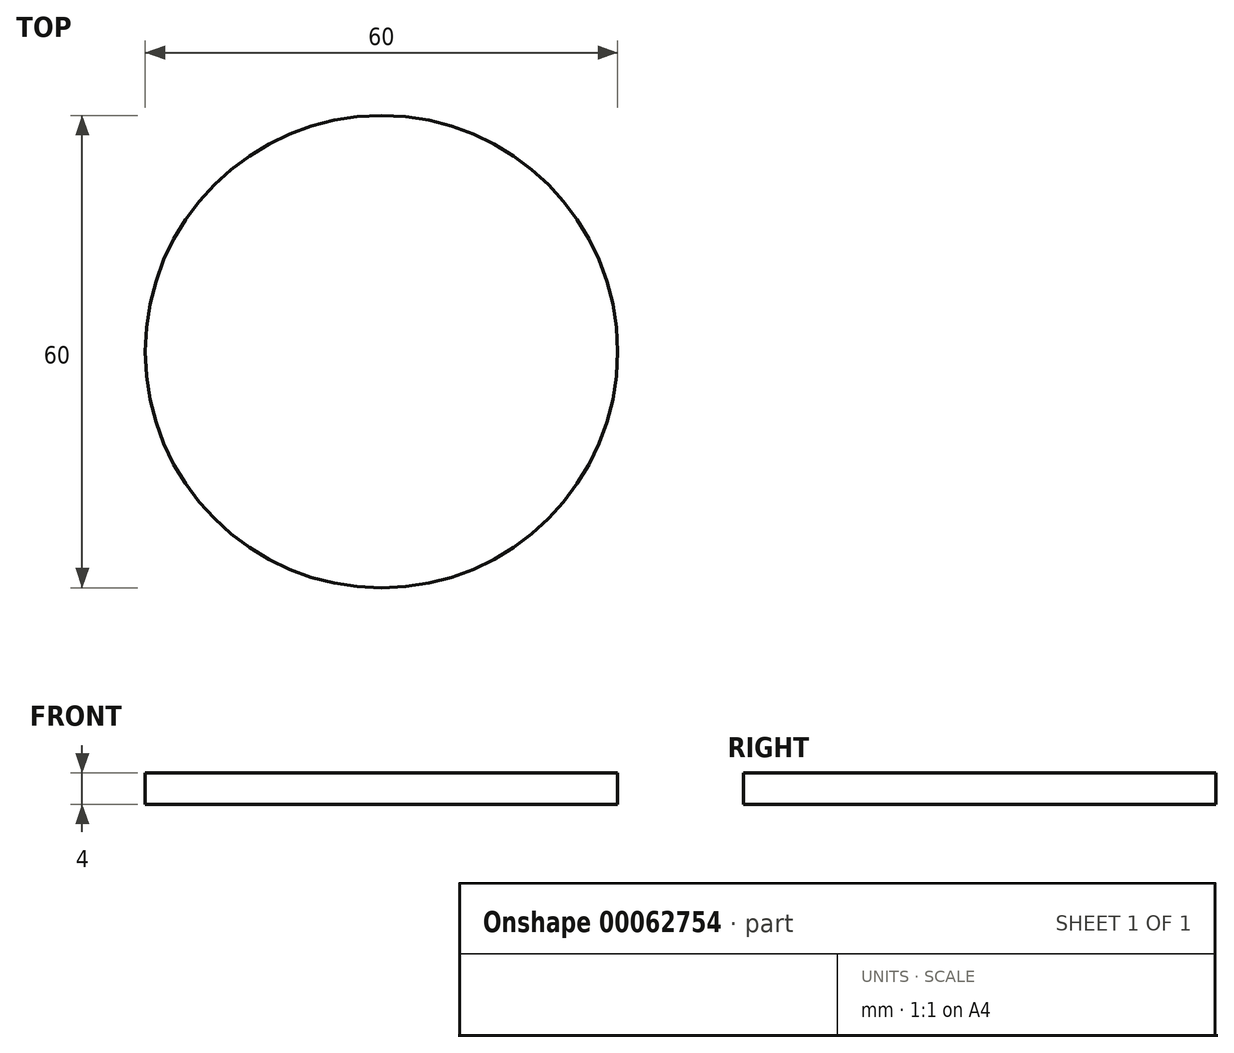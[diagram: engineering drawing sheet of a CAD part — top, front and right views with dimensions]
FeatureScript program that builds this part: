
annotation { "Feature Type Name" : "Feature", "Feature Type Description" : "" }
export const myFeature = defineFeature(function(context is Context, id is Id, definition is map)
    precondition{}
    {
        {
            var Q0;
            Q0=qCreatedBy(makeId("Top.planeOp"),FACE);
            var sketch = newSketch(context, id + "F0", { "sketchPlane" : qUnion([Q0])});
            skCircle(sketch, "E0", {"center": v(0, 0) * mm, "radius": 30 * mm});
            skSolve(sketch);
        }
        {
            var Q0;
            Q0 = qSketchRegion(id + "F0", true);
            extrude(context, id + "F1", {"entities" : qUnion([Q0]), "depth" : 4 * mm});
        }
    });
